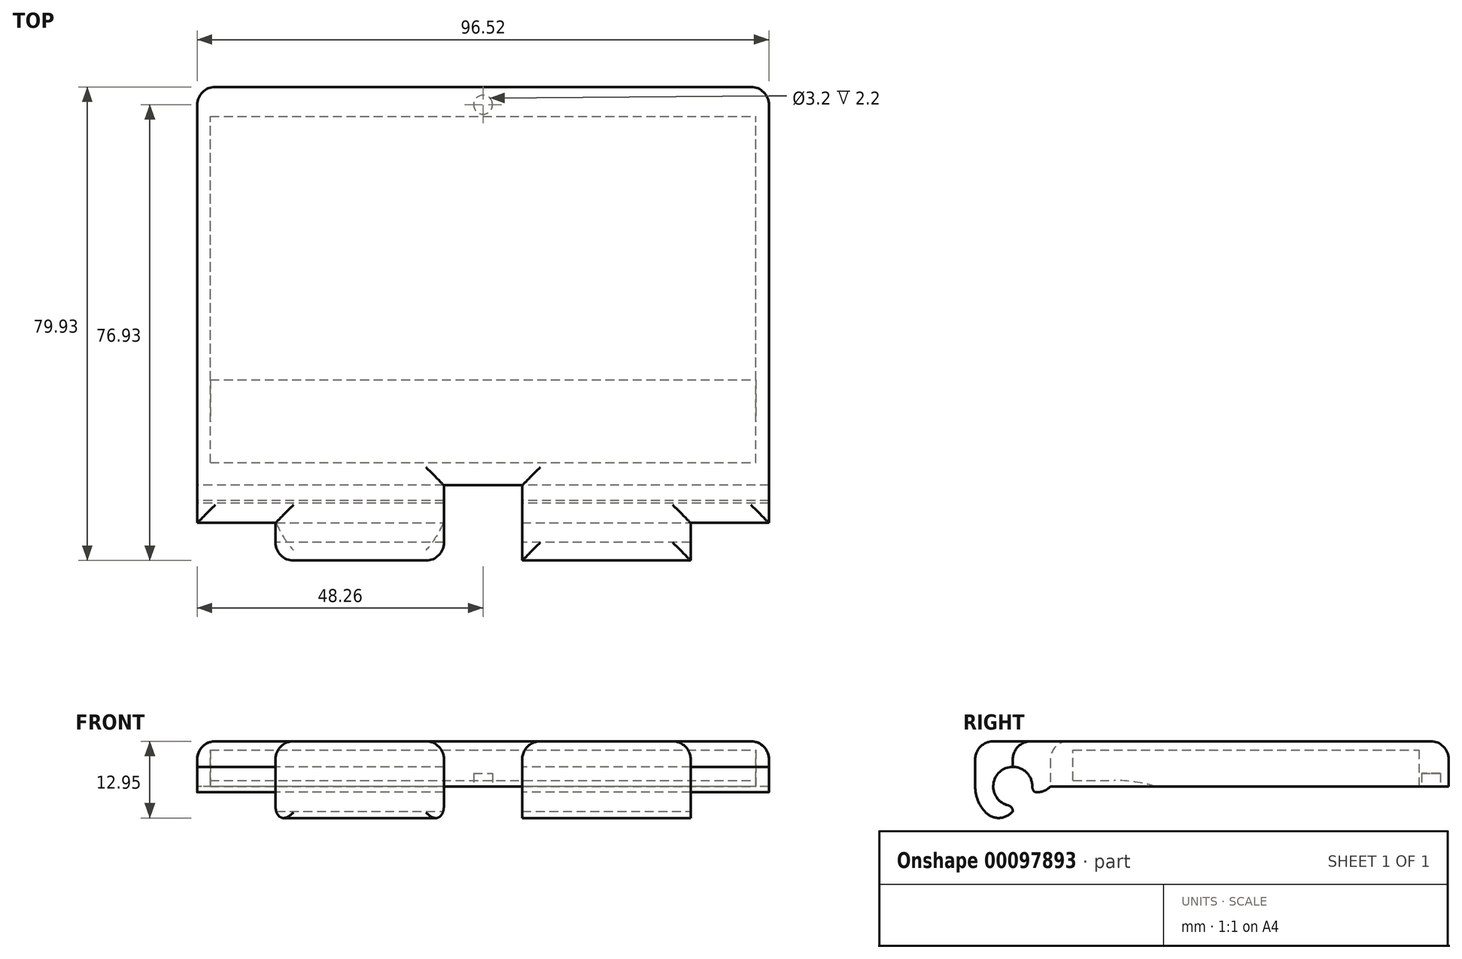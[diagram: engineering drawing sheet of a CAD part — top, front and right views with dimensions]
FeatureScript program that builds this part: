
annotation { "Feature Type Name" : "Feature", "Feature Type Description" : "" }
export const myFeature = defineFeature(function(context is Context, id is Id, definition is map)
    precondition{}
    {
        {
            var Q0;
            Q0=qCreatedBy(makeId("Top.planeOp"),FACE);
            var sketch = newSketch(context, id + "F0", { "sketchPlane" : qUnion([Q0])});
            skLineSegment(sketch, "E0.rect.bottom", {"start": v(48.26, 30.48) * mm, "end": v(-48.26, 30.48) * mm});
            skLineSegment(sketch, "E0.rect.top", {"start": v(48.26, -30.48) * mm, "end": v(-48.26, -30.48) * mm});
            skLineSegment(sketch, "E0.rect.left", {"start": v(48.26, 30.48) * mm, "end": v(48.26, -30.48) * mm});
            skLineSegment(sketch, "E0.rect.right", {"start": v(-48.26, 30.48) * mm, "end": v(-48.26, -30.48) * mm});
            skPoint(sketch, "E0.rect.middle", {"position": v(0, 0) * mm});
            skSolve(sketch);
        }
        {
            var Q0;
            Q0=qSketchRegion(id+"F0",true);
            extrude(context, id + "F1", {"entities" : qUnion([Q0]), "depth" : 7.62 * mm});
        }
        {
            var Q0;
            Q0=qCreatedBy(makeId("Right.planeOp"),FACE);
            var sketch = newSketch(context, id + "F2", { "sketchPlane" : qUnion([Q0])});
            skLineSegment(sketch, "E1", {"start": v(-29.21, 1) * mm, "end": v(-29.21, 6.12) * mm});
            skLineSegment(sketch, "E2", {"start": v(-29.21, 6.12) * mm, "end": v(29.2, 6.12) * mm});
            skLineSegment(sketch, "E3", {"start": v(29.2, 6.12) * mm, "end": v(29.2, 0) * mm});
            skLineSegment(sketch, "E4", {"start": v(-15.24, 0) * mm, "end": v(29.2, 0) * mm});
            skPoint(sketch, "E5.orphan", {"position": v(-29.21, 0) * mm});
            skLineSegment(sketch, "E6", {"start": v(-29.21, 1) * mm, "end": v(-15.24, 1) * mm});
            skLineSegment(sketch, "E7", {"start": v(-15.24, 1) * mm, "end": v(-15.24, 0) * mm});
            skSolve(sketch);
        }
        {
            var Q0;
            Q0=qSketchRegion(id+"F2",true);
            extrude(context, id + "F3", {"entities" : qUnion([Q0]), "operationType" : NewBodyOperationType.REMOVE, "endBound" : BoundingType.SYMMETRIC, "oppositeDirection" : true, "depth" : 92.07 * mm});
        }
        {
            var Q0;
            Q0=makeQuery(id+"F1.opExtrude","SWEPT_FACE",FACE,{"disambiguationData":[OSD([sQuery(id+"F0.wireOp",EDGE,"E0.rect.right")])]});
            var sketch = newSketch(context, id + "F4", { "sketchPlane" : qUnion([Q0])});
            skCircle(sketch, "E8", {"center": v(39.37, 0) * mm, "radius": 6.35 * mm});
            skPoint(sketch, "E8.second.point", {"position": v(33.02, 0) * mm});
            skPoint(sketch, "E8.third.point", {"position": v(39.37, -6.35) * mm});
            skCircle(sketch, "E9", {"center": v(39.37, 0) * mm, "radius": 3.3 * mm});
            skLineSegment(sketch, "E10", {"start": v(39.37, 0) * mm, "end": v(39.37, -6.35) * mm});
            skLineSegment(sketch, "E11", {"start": v(39.37, 0) * mm, "end": v(30.48, 0) * mm});
            skLineSegment(sketch, "E12.bottom", {"start": v(-30.48, 7.62) * mm, "end": v(-34.2, 7.62) * mm});
            skLineSegment(sketch, "E12.top", {"start": v(-30.48, 0) * mm, "end": v(-34.2, 0) * mm});
            skLineSegment(sketch, "E12.left", {"start": v(-30.48, 7.62) * mm, "end": v(-30.48, 0) * mm});
            skLineSegment(sketch, "E12.right", {"start": v(-34.2, 7.62) * mm, "end": v(-34.2, 0) * mm});
            skLineSegment(sketch, "E13.bottom", {"start": v(30.48, 7.62) * mm, "end": v(36.07, 7.62) * mm});
            skLineSegment(sketch, "E13.top", {"start": v(30.48, 0) * mm, "end": v(36.07, 0) * mm, "construction": true});
            skLineSegment(sketch, "E13.left", {"start": v(30.48, 7.62) * mm, "end": v(30.48, 0) * mm});
            skLineSegment(sketch, "E13.right", {"start": v(36.07, 7.62) * mm, "end": v(36.07, 0) * mm});
            skLineSegment(sketch, "E14", {"start": v(39.37, -3.3) * mm, "end": v(44.8, -3.3) * mm});
            skLineSegment(sketch, "E15.0", {"start": v(-29.2, 6.12) * mm, "end": v(-29.21, 0) * mm});
            skLineSegment(sketch, "E16", {"start": v(33.02, 0) * mm, "end": v(30.48, 0) * mm});
            skLineSegment(sketch, "E17", {"start": v(45.72, 0) * mm, "end": v(45.72, 7.62) * mm});
            skLineSegment(sketch, "E18", {"start": v(45.72, 7.62) * mm, "end": v(36.07, 7.62) * mm});
            skLineSegment(sketch, "E19", {"start": v(39.37, 0) * mm, "end": v(33.24, -1.64) * mm});
            skSolve(sketch);
        }
        {
            var Q0;
            {var subQ4=sQuery(id+"F4.wireOp",EDGE,"E13.bottom");Q0=makeQuery(id+"F4.imprint","IMPRINT",FACE,{"disambiguationData":[TD([[makeQuery(id+"F4.imprint","IMPRINT",EDGE,{"derivedFrom":subQ4}),-1.0]])]});}
            var Q1;
            Q1=makeQuery(id+"F4.imprint","IMPRINT",FACE,{"disambiguationData":[TD([[makeQuery(id+"F4.imprint","IMPRINT",EDGE,{"derivedFrom":sQuery(id+"F4.wireOp",EDGE,"E12.bottom")}),1.0]])]});
            var Q2;
            {var subQ0=sQuery(id+"F4.wireOp",EDGE,"E13.right");var subQ1=sQuery(id+"F4.wireOp",EDGE,"E8");var subQ2=makeQuery(id+"F4.imprint","INTERSECT",VERTEX,{"derivedFrom":[subQ1,subQ0]});Q2=makeQuery(id+"F4.imprint","IMPRINT",FACE,{"disambiguationData":[TD([[makeQuery(id+"F4.imprint","IMPRINT",EDGE,{"disambiguationData":[TD([[subQ2,-1.0]])],"derivedFrom":subQ1}),1.0]])]});}
            var Q3;
            {var subQ0=sQuery(id+"F4.wireOp",EDGE,"E14");Q3=makeQuery(id+"F4.imprint","IMPRINT",FACE,{"disambiguationData":[TD([[makeQuery(id+"F4.imprint","IMPRINT",EDGE,{"derivedFrom":subQ0}),-1.0]])]});}
            var Q4;
            {var subQ0=sQuery(id+"F4.wireOp",EDGE,"E14");Q4=makeQuery(id+"F4.imprint","IMPRINT",FACE,{"disambiguationData":[TD([[makeQuery(id+"F4.imprint","IMPRINT",EDGE,{"derivedFrom":subQ0}),1.0]])]});}
            var Q5;
            {var subQ1=sQuery(id+"F4.wireOp",EDGE,"E17");Q5=makeQuery(id+"F4.imprint","IMPRINT",FACE,{"disambiguationData":[TD([[makeQuery(id+"F4.imprint","IMPRINT",EDGE,{"derivedFrom":subQ1}),1.0]])]});}
            var Q6;
            {var subQ0=sQuery(id+"F4.wireOp",EDGE,"E19");var subQ3=sQuery(id+"F4.wireOp",EDGE,"E8");var subQ4=makeQuery(id+"F4.imprint","INTERSECT",VERTEX,{"derivedFrom":[subQ3,subQ0]});Q6=makeQuery(id+"F4.imprint","IMPRINT",FACE,{"disambiguationData":[TD([[makeQuery(id+"F4.imprint","IMPRINT",EDGE,{"disambiguationData":[TD([[subQ4,1.0]])],"derivedFrom":subQ0}),-1.0]])]});}
            var Q7;
            Q7=makeQuery(id+"F1.opExtrude","SWEPT_FACE",FACE,{"disambiguationData":[OSD([sQuery(id+"F0.wireOp",EDGE,"E0.rect.left")])]});
            extrude(context, id + "F5", {"entities" : qUnion([Q0, Q1, Q2, Q3, Q4, Q5, Q6]), "operationType" : NewBodyOperationType.ADD, "endBound" : BoundingType.UP_TO_SURFACE, "oppositeDirection" : true, "endBoundEntityFace" : qUnion([Q7]), "depth" : 25.4 * mm});
        }
        {
            var Q0;
            Q0=makeQuery(id+"F5.boolean.opBoolean","MERGE",FACE,{"derivedFrom":[makeQuery(id+"F1.opExtrude","CAP_FACE",FACE,{"disambiguationData":[OSD([sQuery(id+"F0.wireOp",EDGE,"E0.rect.bottom"),sQuery(id+"F0.wireOp",EDGE,"E0.rect.top"),sQuery(id+"F0.wireOp",EDGE,"E0.rect.left"),sQuery(id+"F0.wireOp",EDGE,"E0.rect.right")])],"isStart":true}),makeQuery(id+"F5.opExtrude","SWEPT_FACE",FACE,{"disambiguationData":[OSD([sQuery(id+"F4.wireOp",EDGE,"E12.top")])]}),makeQuery(id+"F5.opExtrude","SWEPT_FACE",FACE,{"disambiguationData":[OSD([sQuery(id+"F4.wireOp",EDGE,"E16")])]})]});
            var sketch = newSketch(context, id + "F6", { "sketchPlane" : qUnion([Q0])});
            skPoint(sketch, "E20", {"position": v(-48.26, 39.37) * mm});
            skLineSegment(sketch, "E21", {"start": v(-48.26, 39.37) * mm, "end": v(48.26, 39.37) * mm, "construction": true});
            skLineSegment(sketch, "E22.rect.bottom", {"start": v(6.6, 33.02) * mm, "end": v(-6.6, 33.02) * mm});
            skLineSegment(sketch, "E22.rect.top", {"start": v(6.6, 45.72) * mm, "end": v(-6.6, 45.72) * mm});
            skLineSegment(sketch, "E22.rect.left", {"start": v(6.6, 33.02) * mm, "end": v(6.6, 45.72) * mm});
            skLineSegment(sketch, "E22.rect.right", {"start": v(-6.6, 33.02) * mm, "end": v(-6.6, 45.72) * mm});
            skPoint(sketch, "E22.rect.middle", {"position": v(0, 39.37) * mm});
            skLineSegment(sketch, "E23", {"start": v(-20.83, 31.11) * mm, "end": v(-20.83, 47.62) * mm, "construction": true});
            skPoint(sketch, "E24", {"position": v(-20.83, 39.37) * mm});
            skLineSegment(sketch, "E25", {"start": v(-48.26, 39.37) * mm, "end": v(6.6, 39.37) * mm, "construction": true});
            skLineSegment(sketch, "E26", {"start": v(48.26, 39.37) * mm, "end": v(-6.6, 39.37) * mm, "construction": true});
            skLineSegment(sketch, "E27.0.MirrorCS", {"start": v(-35.05, 33.02) * mm, "end": v(-35.05, 45.72) * mm});
            skLineSegment(sketch, "E28.0.MirrorCS", {"start": v(-48.26, 45.72) * mm, "end": v(-35.05, 45.72) * mm});
            skLineSegment(sketch, "E29.0.MirrorCS", {"start": v(-48.26, 33.02) * mm, "end": v(-48.26, 45.72) * mm});
            skLineSegment(sketch, "E30.0.MirrorCS", {"start": v(-48.26, 33.02) * mm, "end": v(-35.05, 33.02) * mm});
            skLineSegment(sketch, "E31", {"start": v(20.83, 47.62) * mm, "end": v(20.83, 31.11) * mm, "construction": true});
            skPoint(sketch, "E32", {"position": v(20.83, 39.37) * mm});
            skLineSegment(sketch, "E33.0.MirrorCS", {"start": v(35.05, 33.02) * mm, "end": v(48.26, 33.02) * mm});
            skLineSegment(sketch, "E33.1.MirrorCS", {"start": v(48.26, 33.02) * mm, "end": v(48.26, 45.72) * mm});
            skPoint(sketch, "E33.2.MirrorP", {"position": v(41.66, 39.37) * mm});
            skLineSegment(sketch, "E33.3.MirrorCS", {"start": v(35.05, 45.72) * mm, "end": v(48.26, 45.72) * mm});
            skLineSegment(sketch, "E33.4.MirrorCS", {"start": v(35.05, 33.02) * mm, "end": v(35.05, 45.72) * mm});
            skLineSegment(sketch, "E34.0.0", {"start": v(-48.26, 39.37) * mm, "end": v(48.26, 39.37) * mm});
            skLineSegment(sketch, "E34.0.1", {"start": v(48.26, 39.37) * mm, "end": v(48.26, 45.72) * mm});
            skLineSegment(sketch, "E34.0.2", {"start": v(-48.26, 39.37) * mm, "end": v(48.26, 39.37) * mm});
            skLineSegment(sketch, "E34.0.3", {"start": v(-48.26, 45.72) * mm, "end": v(-48.26, 39.37) * mm});
            skSolve(sketch);
        }
        {
            var Q0;
            {var subQ1=sQuery(id+"F6.wireOp",EDGE,"E27.0.MirrorCS");var subQ5=sQuery(id+"F6.wireOp",EDGE,"E34.0.2");var subQ6=makeQuery(id+"F6.imprint","INTERSECT",VERTEX,{"derivedFrom":[subQ1,subQ5]});Q0=makeQuery(id+"F6.imprint","IMPRINT",FACE,{"disambiguationData":[TD([[makeQuery(id+"F6.imprint","IMPRINT",EDGE,{"disambiguationData":[TD([[subQ6,1.0]])],"derivedFrom":subQ5}),-1.0]])]});}
            var Q1;
            {var subQ3=sQuery(id+"F6.wireOp",EDGE,"E22.rect.left");var subQ5=sQuery(id+"F6.wireOp",EDGE,"E34.0.2");var subQ7=makeQuery(id+"F6.imprint","INTERSECT",VERTEX,{"derivedFrom":[subQ3,subQ5]});Q1=makeQuery(id+"F6.imprint","IMPRINT",FACE,{"disambiguationData":[TD([[makeQuery(id+"F6.imprint","IMPRINT",EDGE,{"disambiguationData":[TD([[subQ7,1.0]])],"derivedFrom":subQ5}),-1.0]])]});}
            var Q2;
            {var subQ5=sQuery(id+"F6.wireOp",EDGE,"E22.rect.bottom");Q2=makeQuery(id+"F6.imprint","IMPRINT",FACE,{"disambiguationData":[TD([[makeQuery(id+"F6.imprint","IMPRINT",EDGE,{"derivedFrom":subQ5}),-1.0]])]});}
            var Q3;
            {var subQ1=sQuery(id+"F6.wireOp",EDGE,"E33.4.MirrorCS");var subQ5=sQuery(id+"F6.wireOp",EDGE,"E34.0.2");var subQ6=makeQuery(id+"F6.imprint","INTERSECT",VERTEX,{"derivedFrom":[subQ1,subQ5]});Q3=makeQuery(id+"F6.imprint","IMPRINT",FACE,{"disambiguationData":[TD([[makeQuery(id+"F6.imprint","IMPRINT",EDGE,{"disambiguationData":[TD([[subQ6,-1.0]])],"derivedFrom":subQ5}),-1.0]])]});}
            var Q4;
            {var subQ5=sQuery(id+"F6.wireOp",EDGE,"E22.rect.top");Q4=makeQuery(id+"F6.imprint","IMPRINT",FACE,{"disambiguationData":[TD([[makeQuery(id+"F6.imprint","IMPRINT",EDGE,{"derivedFrom":subQ5}),1.0]])]});}
            var Q5;
            {var subQ5=sQuery(id+"F6.wireOp",EDGE,"E33.3.MirrorCS");Q5=makeQuery(id+"F6.imprint","IMPRINT",FACE,{"disambiguationData":[TD([[makeQuery(id+"F6.imprint","IMPRINT",EDGE,{"derivedFrom":subQ5}),-1.0]])]});}
            var Q6;
            {var subQ5=sQuery(id+"F6.wireOp",EDGE,"E28.0.MirrorCS");Q6=makeQuery(id+"F6.imprint","IMPRINT",FACE,{"disambiguationData":[TD([[makeQuery(id+"F6.imprint","IMPRINT",EDGE,{"derivedFrom":subQ5}),-1.0]])]});}
            extrude(context, id + "F7", {"entities" : qUnion([Q0, Q1, Q2, Q3, Q4, Q5, Q6]), "operationType" : NewBodyOperationType.REMOVE, "endBound" : BoundingType.THROUGH_ALL, "oppositeDirection" : true, "depth" : 25.4 * mm, "hasSecondDirection" : true, "secondDirectionBound" : SecondDirectionBoundingType.THROUGH_ALL, "secondDirectionOppositeDirection" : false, "secondDirectionDepth" : 25.4 * mm});
        }
        {
            var Q0;
            Q0=makeQuery(id+"F5.boolean.opBoolean","MERGE",FACE,{"derivedFrom":[makeQuery(id+"F1.opExtrude","CAP_FACE",FACE,{"disambiguationData":[OSD([sQuery(id+"F0.wireOp",EDGE,"E0.rect.bottom"),sQuery(id+"F0.wireOp",EDGE,"E0.rect.top"),sQuery(id+"F0.wireOp",EDGE,"E0.rect.left"),sQuery(id+"F0.wireOp",EDGE,"E0.rect.right")])],"isStart":true}),makeQuery(id+"F5.opExtrude","SWEPT_FACE",FACE,{"disambiguationData":[OSD([sQuery(id+"F4.wireOp",EDGE,"E12.top")])]}),makeQuery(id+"F5.opExtrude","SWEPT_FACE",FACE,{"disambiguationData":[OSD([sQuery(id+"F4.wireOp",EDGE,"E16")])]})]});
            var sketch = newSketch(context, id + "F8", { "sketchPlane" : qUnion([Q0])});
            skCircle(sketch, "E35", {"center": v(0, -31.21) * mm, "radius": 1.6 * mm});
            skSolve(sketch);
        }
        {
            var Q0;
            Q0=makeQuery(id+"F8.imprint","IMPRINT",FACE,{"disambiguationData":[TD([[makeQuery(id+"F8.imprint","IMPRINT",EDGE,{"derivedFrom":sQuery(id+"F8.wireOp",EDGE,"E35")}),1.0]])]});
            extrude(context, id + "F9", {"entities" : qUnion([Q0]), "operationType" : NewBodyOperationType.REMOVE, "oppositeDirection" : true, "depth" : 2.2 * mm});
        }
        {
            var Q0;
            {var subQ0=sQuery(id+"F4.wireOp",EDGE,"E9");var subQ1=sQuery(id+"F4.wireOp",EDGE,"E19");Q0=makeQuery(id+"F7.boolean.opBoolean","SPLIT",EDGE,{"disambiguationData":[TD([makeQuery(id+"F7.opExtrude","SWEPT_FACE",FACE,{"disambiguationData":[OSD([sQuery(id+"F6.wireOp",EDGE,"E22.rect.left")])]})])],"derivedFrom":makeQuery(id+"F5.opExtrude","SWEPT_EDGE",EDGE,{"disambiguationData":[OSD([subQ0,subQ1])]})});}
            var Q1;
            {var subQ0=sQuery(id+"F4.wireOp",EDGE,"E9");var subQ1=sQuery(id+"F4.wireOp",EDGE,"E19");Q1=makeQuery(id+"F7.boolean.opBoolean","SPLIT",EDGE,{"disambiguationData":[TD([makeQuery(id+"F7.opExtrude","SWEPT_FACE",FACE,{"disambiguationData":[OSD([sQuery(id+"F6.wireOp",EDGE,"E22.rect.right")])]})])],"derivedFrom":makeQuery(id+"F5.opExtrude","SWEPT_EDGE",EDGE,{"disambiguationData":[OSD([subQ0,subQ1])]})});}
            var Q2;
            {var subQ0=sQuery(id+"F4.wireOp",EDGE,"E9");var subQ1=sQuery(id+"F4.wireOp",EDGE,"E10");Q2=makeQuery(id+"F7.boolean.opBoolean","SPLIT",EDGE,{"disambiguationData":[TD([makeQuery(id+"F7.opExtrude","SWEPT_FACE",FACE,{"disambiguationData":[OSD([sQuery(id+"F6.wireOp",EDGE,"E22.rect.left")])]})])],"derivedFrom":makeQuery(id+"F5.opExtrude","SWEPT_EDGE",EDGE,{"disambiguationData":[OSD([subQ0,subQ1,sQuery(id+"F4.wireOp",EDGE,"E14")])]})});}
            var Q3;
            {var subQ0=sQuery(id+"F4.wireOp",EDGE,"E9");var subQ1=sQuery(id+"F4.wireOp",EDGE,"E10");Q3=makeQuery(id+"F7.boolean.opBoolean","SPLIT",EDGE,{"disambiguationData":[TD([makeQuery(id+"F7.opExtrude","SWEPT_FACE",FACE,{"disambiguationData":[OSD([sQuery(id+"F6.wireOp",EDGE,"E22.rect.right")])]})])],"derivedFrom":makeQuery(id+"F5.opExtrude","SWEPT_EDGE",EDGE,{"disambiguationData":[OSD([subQ0,subQ1,sQuery(id+"F4.wireOp",EDGE,"E14")])]})});}
            fillet(context, id + "F10", {"entities" : qUnion([Q0, Q1, Q2, Q3]), "radius" : 1 * mm, "tangentPropagation" : true, "allowEdgeOverflow" : false});
        }
        {
            var Q0;
            Q0=makeQuery(id+"F5.boolean.opBoolean","MERGE",FACE,{"derivedFrom":[makeQuery(id+"F1.opExtrude","CAP_FACE",FACE,{"disambiguationData":[OSD([sQuery(id+"F0.wireOp",EDGE,"E0.rect.bottom"),sQuery(id+"F0.wireOp",EDGE,"E0.rect.top"),sQuery(id+"F0.wireOp",EDGE,"E0.rect.left"),sQuery(id+"F0.wireOp",EDGE,"E0.rect.right")])],"isStart":false}),makeQuery(id+"F5.opExtrude","SWEPT_FACE",FACE,{"disambiguationData":[OSD([sQuery(id+"F4.wireOp",EDGE,"E12.bottom")])]}),makeQuery(id+"F5.opExtrude","SWEPT_FACE",FACE,{"disambiguationData":[OSD([sQuery(id+"F4.wireOp",EDGE,"E13.bottom"),sQuery(id+"F4.wireOp",EDGE,"E18")])]})]});
            var Q1;
            {var subQ0=sQuery(id+"F4.wireOp",EDGE,"E8");var subQ1=sQuery(id+"F4.wireOp",EDGE,"E19");Q1=makeQuery(id+"F7.boolean.opBoolean","SPLIT",EDGE,{"disambiguationData":[TD([makeQuery(id+"F7.opExtrude","SWEPT_FACE",FACE,{"disambiguationData":[OSD([sQuery(id+"F6.wireOp",EDGE,"E22.rect.right")])]})])],"derivedFrom":makeQuery(id+"F5.opExtrude","SWEPT_EDGE",EDGE,{"disambiguationData":[OSD([subQ0,subQ1])]})});}
            var Q2;
            {var subQ0=sQuery(id+"F4.wireOp",EDGE,"E8");var subQ1=sQuery(id+"F4.wireOp",EDGE,"E19");Q2=makeQuery(id+"F7.boolean.opBoolean","SPLIT",EDGE,{"disambiguationData":[TD([makeQuery(id+"F7.opExtrude","SWEPT_FACE",FACE,{"disambiguationData":[OSD([sQuery(id+"F6.wireOp",EDGE,"E22.rect.left")])]})])],"derivedFrom":makeQuery(id+"F5.opExtrude","SWEPT_EDGE",EDGE,{"disambiguationData":[OSD([subQ0,subQ1])]})});}
            var Q3;
            {var subQ0=sQuery(id+"F4.wireOp",EDGE,"E8");var subQ2=sQuery(id+"F4.wireOp",EDGE,"E10");Q3=makeQuery(id+"F7.boolean.opBoolean","SPLIT",EDGE,{"disambiguationData":[TD([makeQuery(id+"F7.opExtrude","SWEPT_FACE",FACE,{"disambiguationData":[OSD([sQuery(id+"F6.wireOp",EDGE,"E22.rect.left")])]})])],"derivedFrom":makeQuery(id+"F5.opExtrude","SWEPT_EDGE",EDGE,{"disambiguationData":[OSD([subQ0,subQ2])]})});}
            var Q4;
            {var subQ0=sQuery(id+"F4.wireOp",EDGE,"E8");var subQ2=sQuery(id+"F4.wireOp",EDGE,"E10");Q4=makeQuery(id+"F7.boolean.opBoolean","SPLIT",EDGE,{"disambiguationData":[TD([makeQuery(id+"F7.opExtrude","SWEPT_FACE",FACE,{"disambiguationData":[OSD([sQuery(id+"F6.wireOp",EDGE,"E22.rect.right")])]})])],"derivedFrom":makeQuery(id+"F5.opExtrude","SWEPT_EDGE",EDGE,{"disambiguationData":[OSD([subQ0,subQ2])]})});}
            var Q5;
            {var subQ0=sQuery(id+"F4.wireOp",EDGE,"E8");var subQ1=makeQuery(id+"F4.imprint","INTERSECT",VERTEX,{"derivedFrom":[subQ0,sQuery(id+"F4.wireOp",EDGE,"E14")]});Q5=makeQuery(id+"F7.boolean.opBoolean","INTERSECT",EDGE,{"derivedFrom":[makeQuery(id+"F5.opExtrude","SWEPT_FACE",FACE,{"disambiguationData":[OSD([subQ0]),TDD([makeQuery(id+"F4.imprint","IMPRINT",EDGE,{"disambiguationData":[TD([[makeQuery(id+"F4.imprint","INTERSECT",VERTEX,{"derivedFrom":[subQ0,sQuery(id+"F4.wireOp",EDGE,"E10")]}),-1.0]])],"derivedFrom":subQ0}),makeQuery(id+"F4.imprint","IMPRINT",EDGE,{"disambiguationData":[TD([[subQ1,-1.0]])],"derivedFrom":subQ0})])]}),makeQuery(id+"F7.opExtrude","SWEPT_FACE",FACE,{"disambiguationData":[OSD([sQuery(id+"F6.wireOp",EDGE,"E27.0.MirrorCS")])]})]});}
            var Q6;
            Q6=makeQuery(id+"F7.boolean.opBoolean","COPY",EDGE,{"derivedFrom":makeQuery(id+"F7.opExtrude","SWEPT_EDGE",EDGE,{"disambiguationData":[OSD([sQuery(id+"F6.wireOp",EDGE,"E22.rect.top"),sQuery(id+"F6.wireOp",EDGE,"E22.rect.left")])]})});
            var Q7;
            Q7=makeQuery(id+"F7.boolean.opBoolean","COPY",EDGE,{"derivedFrom":makeQuery(id+"F7.opExtrude","SWEPT_EDGE",EDGE,{"disambiguationData":[OSD([sQuery(id+"F6.wireOp",EDGE,"E33.3.MirrorCS"),sQuery(id+"F6.wireOp",EDGE,"E33.4.MirrorCS")])]})});
            var Q8;
            Q8=makeQuery(id+"F7.boolean.opBoolean","COPY",EDGE,{"derivedFrom":makeQuery(id+"F7.opExtrude","SWEPT_EDGE",EDGE,{"disambiguationData":[OSD([sQuery(id+"F6.wireOp",EDGE,"E22.rect.top"),sQuery(id+"F6.wireOp",EDGE,"E22.rect.right")])]})});
            fillet(context, id + "F11", {"entities" : qUnion([Q0, Q1, Q2, Q3, Q4, Q5, Q6, Q7, Q8]), "radius" : 3.05 * mm, "tangentPropagation" : true, "allowEdgeOverflow" : false});
        }
        {
            var Q0;
            {var subQ0=sQuery(id+"F4.wireOp",EDGE,"E16");Q0=makeQuery(id+"F7.boolean.opBoolean","SPLIT",EDGE,{"disambiguationData":[topologyDisambiguationEdgeConnected([makeQuery(id+"F1.opExtrude","CAP_FACE",FACE,{"disambiguationData":[OSD([sQuery(id+"F0.wireOp",EDGE,"E0.rect.bottom"),sQuery(id+"F0.wireOp",EDGE,"E0.rect.top"),sQuery(id+"F0.wireOp",EDGE,"E0.rect.left"),sQuery(id+"F0.wireOp",EDGE,"E0.rect.right")])],"isStart":true}),makeQuery(id+"F5.opExtrude","SWEPT_FACE",FACE,{"disambiguationData":[OSD([sQuery(id+"F4.wireOp",EDGE,"E12.top")])]}),makeQuery(id+"F5.opExtrude","SWEPT_FACE",FACE,{"disambiguationData":[OSD([subQ0])]}),makeQuery(id+"F7.opExtrude","SWEPT_FACE",FACE,{"disambiguationData":[OSD([sQuery(id+"F6.wireOp",EDGE,"E22.rect.bottom")])]})])],"derivedFrom":makeQuery(id+"F5.opExtrude","SWEPT_EDGE",EDGE,{"disambiguationData":[OSD([sQuery(id+"F4.wireOp",EDGE,"E8"),sQuery(id+"F4.wireOp",EDGE,"E11"),subQ0])]})});}
            var Q1;
            {var subQ0=sQuery(id+"F4.wireOp",EDGE,"E16");Q1=makeQuery(id+"F7.boolean.opBoolean","SPLIT",EDGE,{"disambiguationData":[topologyDisambiguationEdgeConnected([makeQuery(id+"F1.opExtrude","CAP_FACE",FACE,{"disambiguationData":[OSD([sQuery(id+"F0.wireOp",EDGE,"E0.rect.bottom"),sQuery(id+"F0.wireOp",EDGE,"E0.rect.top"),sQuery(id+"F0.wireOp",EDGE,"E0.rect.left"),sQuery(id+"F0.wireOp",EDGE,"E0.rect.right")])],"isStart":true}),makeQuery(id+"F5.opExtrude","SWEPT_FACE",FACE,{"disambiguationData":[OSD([sQuery(id+"F4.wireOp",EDGE,"E12.top")])]}),makeQuery(id+"F5.opExtrude","SWEPT_FACE",FACE,{"disambiguationData":[OSD([subQ0])]}),makeQuery(id+"F7.opExtrude","SWEPT_FACE",FACE,{"disambiguationData":[OSD([sQuery(id+"F6.wireOp",EDGE,"E33.0.MirrorCS")])]})])],"derivedFrom":makeQuery(id+"F5.opExtrude","SWEPT_EDGE",EDGE,{"disambiguationData":[OSD([sQuery(id+"F4.wireOp",EDGE,"E8"),sQuery(id+"F4.wireOp",EDGE,"E11"),subQ0])]})});}
            var Q2;
            {var subQ0=sQuery(id+"F4.wireOp",EDGE,"E16");Q2=makeQuery(id+"F7.boolean.opBoolean","SPLIT",EDGE,{"disambiguationData":[topologyDisambiguationEdgeConnected([makeQuery(id+"F1.opExtrude","CAP_FACE",FACE,{"disambiguationData":[OSD([sQuery(id+"F0.wireOp",EDGE,"E0.rect.bottom"),sQuery(id+"F0.wireOp",EDGE,"E0.rect.top"),sQuery(id+"F0.wireOp",EDGE,"E0.rect.left"),sQuery(id+"F0.wireOp",EDGE,"E0.rect.right")])],"isStart":true}),makeQuery(id+"F5.opExtrude","SWEPT_FACE",FACE,{"disambiguationData":[OSD([sQuery(id+"F4.wireOp",EDGE,"E12.top")])]}),makeQuery(id+"F5.opExtrude","SWEPT_FACE",FACE,{"disambiguationData":[OSD([subQ0])]}),makeQuery(id+"F7.opExtrude","SWEPT_FACE",FACE,{"disambiguationData":[OSD([sQuery(id+"F6.wireOp",EDGE,"E30.0.MirrorCS")])]})])],"derivedFrom":makeQuery(id+"F5.opExtrude","SWEPT_EDGE",EDGE,{"disambiguationData":[OSD([sQuery(id+"F4.wireOp",EDGE,"E8"),sQuery(id+"F4.wireOp",EDGE,"E11"),subQ0])]})});}
            var Q3;
            Q3=makeQuery(id+"F5.opExtrude","CAP_EDGE",EDGE,{"disambiguationData":[OSD([sQuery(id+"F4.wireOp",EDGE,"E12.right")])],"isStart":false});
            var Q4;
            Q4=makeQuery(id+"F7.boolean.opBoolean","COPY",EDGE,{"derivedFrom":makeQuery(id+"F7.opExtrude","SWEPT_EDGE",EDGE,{"disambiguationData":[OSD([sQuery(id+"F0.wireOp",EDGE,"E0.rect.left"),sQuery(id+"F4.wireOp",EDGE,"E12.top"),sQuery(id+"F4.wireOp",EDGE,"E16"),sQuery(id+"F6.wireOp",EDGE,"E33.0.MirrorCS"),sQuery(id+"F6.wireOp",EDGE,"E33.1.MirrorCS")])]})});
            var Q5;
            Q5=makeQuery(id+"F7.boolean.opBoolean","COPY",EDGE,{"derivedFrom":makeQuery(id+"F7.opExtrude","SWEPT_EDGE",EDGE,{"disambiguationData":[OSD([sQuery(id+"F0.wireOp",EDGE,"E0.rect.right"),sQuery(id+"F4.wireOp",EDGE,"E12.top"),sQuery(id+"F4.wireOp",EDGE,"E16"),sQuery(id+"F6.wireOp",EDGE,"E29.0.MirrorCS"),sQuery(id+"F6.wireOp",EDGE,"E30.0.MirrorCS")])]})});
            var Q6;
            Q6=makeQuery(id+"F5.opExtrude","CAP_EDGE",EDGE,{"disambiguationData":[OSD([sQuery(id+"F4.wireOp",EDGE,"E12.right")])],"isStart":true});
            fillet(context, id + "F12", {"entities" : qUnion([Q0, Q1, Q2, Q3, Q4, Q5, Q6]), "radius" : 3.05 * mm, "tangentPropagation" : true, "allowEdgeOverflow" : false});
        }
        {
            var Q0;
            Q0=makeQuery(id+"F3.boolean.opBoolean","COPY",EDGE,{"derivedFrom":makeQuery(id+"F3.opExtrude","SWEPT_EDGE",EDGE,{"disambiguationData":[OSD([sQuery(id+"F2.wireOp",EDGE,"E6"),sQuery(id+"F2.wireOp",EDGE,"E7")])]})});
            fillet(context, id + "F13", {"entities" : qUnion([Q0]), "radius" : 25.4 * mm, "tangentPropagation" : true, "allowEdgeOverflow" : false});
        }
    });
